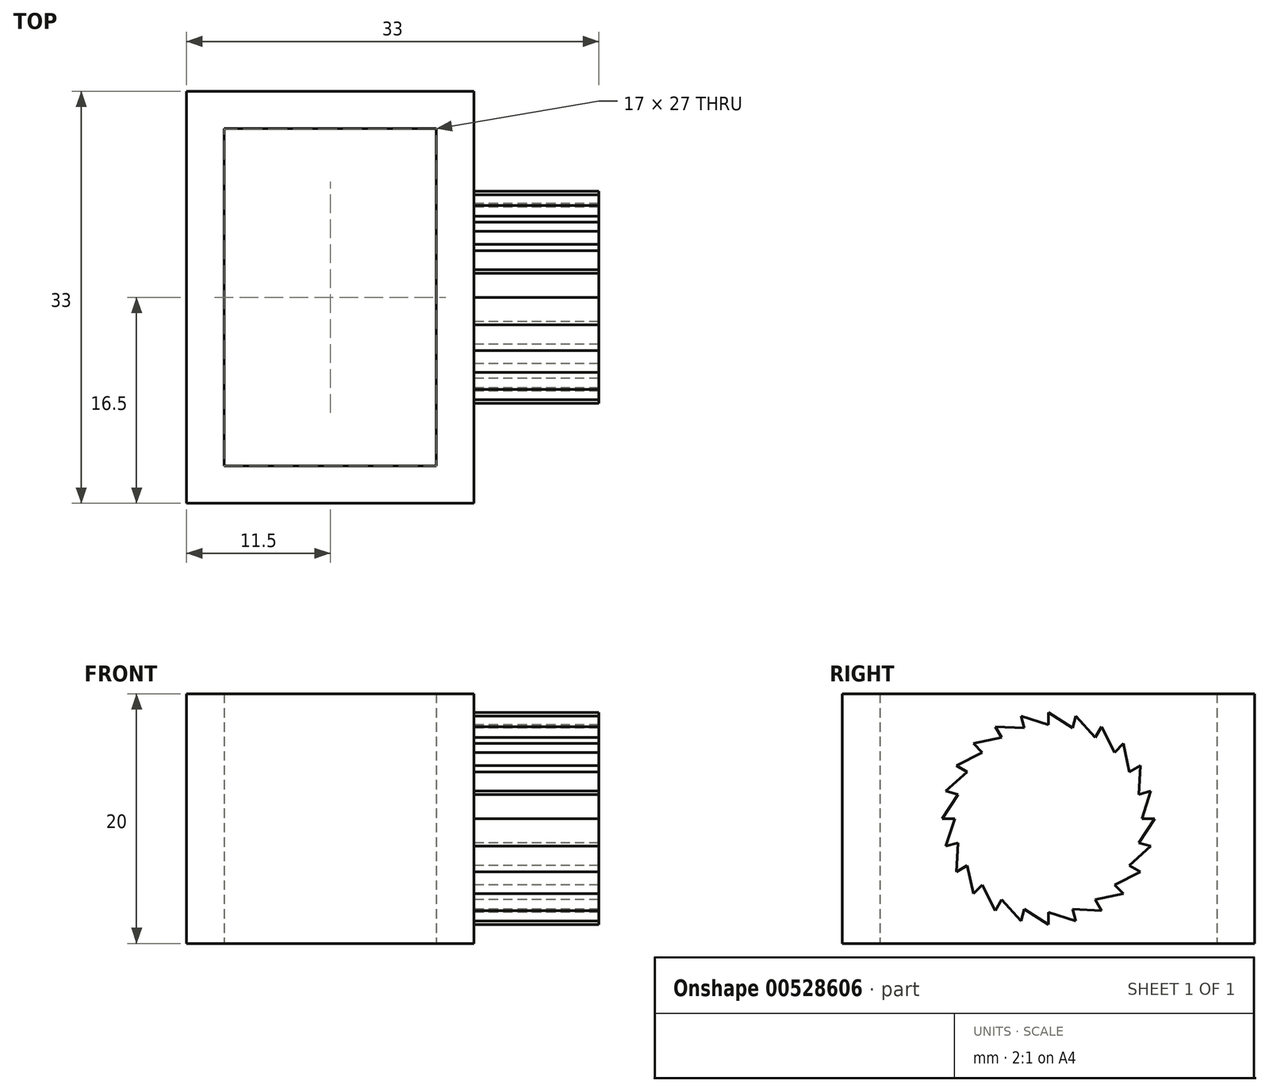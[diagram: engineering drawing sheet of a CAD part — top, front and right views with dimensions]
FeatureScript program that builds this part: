
annotation { "Feature Type Name" : "Feature", "Feature Type Description" : "" }
export const myFeature = defineFeature(function(context is Context, id is Id, definition is map)
    precondition{}
    {
        {
            var Q0;
            Q0=qCreatedBy(makeId("Top.planeOp"),FACE);
            var sketch = newSketch(context, id + "F0", { "sketchPlane" : qUnion([Q0])});
            skLineSegment(sketch, "E0.bottom", {"start": v(3, 3) * mm, "end": v(20, 3) * mm});
            skLineSegment(sketch, "E0.top", {"start": v(3, 30) * mm, "end": v(20, 30) * mm});
            skLineSegment(sketch, "E0.left", {"start": v(3, 3) * mm, "end": v(3, 30) * mm});
            skLineSegment(sketch, "E0.right", {"start": v(20, 3) * mm, "end": v(20, 30) * mm});
            skLineSegment(sketch, "E1.0", {"start": v(23, 0) * mm, "end": v(23, 33) * mm});
            skLineSegment(sketch, "E1.1", {"start": v(0, 0) * mm, "end": v(23, 0) * mm});
            skLineSegment(sketch, "E1.2", {"start": v(0, 0) * mm, "end": v(0, 33) * mm});
            skLineSegment(sketch, "E1.3", {"start": v(0, 33) * mm, "end": v(23, 33) * mm});
            skSolve(sketch);
        }
        {
            var Q0;
            Q0=makeQuery(id+"F0.imprint","IMPRINT",FACE,{"disambiguationData":[TD([[makeQuery(id+"F0.imprint","IMPRINT",EDGE,{"derivedFrom":sQuery(id+"F0.wireOp",EDGE,"E0.bottom")}),-1.0]])]});
            extrude(context, id + "F1", {"entities" : qUnion([Q0]), "depth" : 20 * mm, "offsetDistance" : 25 * mm});
        }
        {
            var Q0;
            Q0=makeQuery(id+"F1.opExtrude","SWEPT_FACE",FACE,{"disambiguationData":[OSD([sQuery(id+"F0.wireOp",EDGE,"E1.0")])]});
            var sketch = newSketch(context, id + "F2", { "sketchPlane" : qUnion([Q0])});
            skCircle(sketch, "E2", {"center": v(16.5, 10) * mm, "radius": 7.5 * mm});
            skLineSegment(sketch, "E3", {"start": v(16.5, 17.5) * mm, "end": v(16.5, 18.5) * mm});
            skLineSegment(sketch, "E4", {"start": v(16.5, 18.5) * mm, "end": v(18.44, 17.24) * mm});
            skLineSegment(sketch, "E5.1.0", {"start": v(18.7, 18.21) * mm, "end": v(20.25, 16.5) * mm});
            skLineSegment(sketch, "E5.1.1", {"start": v(18.44, 17.24) * mm, "end": v(18.7, 18.21) * mm});
            skLineSegment(sketch, "E5.2.0", {"start": v(20.75, 17.36) * mm, "end": v(21.8, 15.3) * mm});
            skLineSegment(sketch, "E5.2.1", {"start": v(20.25, 16.5) * mm, "end": v(20.75, 17.36) * mm});
            skLineSegment(sketch, "E5.3.0", {"start": v(22.51, 16.01) * mm, "end": v(23, 13.75) * mm});
            skLineSegment(sketch, "E5.3.1", {"start": v(21.8, 15.3) * mm, "end": v(22.51, 16.01) * mm});
            skLineSegment(sketch, "E5.4.0", {"start": v(23.86, 14.25) * mm, "end": v(23.74, 11.94) * mm});
            skLineSegment(sketch, "E5.4.1", {"start": v(23, 13.75) * mm, "end": v(23.86, 14.25) * mm});
            skLineSegment(sketch, "E5.5.0", {"start": v(24.71, 12.2) * mm, "end": v(24, 10) * mm});
            skLineSegment(sketch, "E5.5.1", {"start": v(23.74, 11.94) * mm, "end": v(24.71, 12.2) * mm});
            skLineSegment(sketch, "E5.6.0", {"start": v(25, 10) * mm, "end": v(23.74, 8.06) * mm});
            skLineSegment(sketch, "E5.6.1", {"start": v(24, 10) * mm, "end": v(25, 10) * mm});
            skLineSegment(sketch, "E5.7.0", {"start": v(24.71, 7.8) * mm, "end": v(23, 6.25) * mm});
            skLineSegment(sketch, "E5.7.1", {"start": v(23.74, 8.06) * mm, "end": v(24.71, 7.8) * mm});
            skLineSegment(sketch, "E5.8.0", {"start": v(23.86, 5.75) * mm, "end": v(21.8, 4.7) * mm});
            skLineSegment(sketch, "E5.8.1", {"start": v(23, 6.25) * mm, "end": v(23.86, 5.75) * mm});
            skLineSegment(sketch, "E5.9.0", {"start": v(22.51, 3.99) * mm, "end": v(20.25, 3.5) * mm});
            skLineSegment(sketch, "E5.9.1", {"start": v(21.8, 4.7) * mm, "end": v(22.51, 3.99) * mm});
            skLineSegment(sketch, "E5.10.0", {"start": v(20.75, 2.64) * mm, "end": v(18.44, 2.76) * mm});
            skLineSegment(sketch, "E5.10.1", {"start": v(20.25, 3.5) * mm, "end": v(20.75, 2.64) * mm});
            skLineSegment(sketch, "E5.11.0", {"start": v(18.7, 1.79) * mm, "end": v(16.5, 2.5) * mm});
            skLineSegment(sketch, "E5.11.1", {"start": v(18.44, 2.76) * mm, "end": v(18.7, 1.79) * mm});
            skLineSegment(sketch, "E5.12.0", {"start": v(16.5, 1.5) * mm, "end": v(14.56, 2.76) * mm});
            skLineSegment(sketch, "E5.12.1", {"start": v(16.5, 2.5) * mm, "end": v(16.5, 1.5) * mm});
            skLineSegment(sketch, "E5.13.0", {"start": v(14.3, 1.79) * mm, "end": v(12.75, 3.5) * mm});
            skLineSegment(sketch, "E5.13.1", {"start": v(14.56, 2.76) * mm, "end": v(14.3, 1.79) * mm});
            skLineSegment(sketch, "E5.14.0", {"start": v(12.25, 2.64) * mm, "end": v(11.2, 4.7) * mm});
            skLineSegment(sketch, "E5.14.1", {"start": v(12.75, 3.5) * mm, "end": v(12.25, 2.64) * mm});
            skLineSegment(sketch, "E5.15.0", {"start": v(10.49, 3.99) * mm, "end": v(10, 6.25) * mm});
            skLineSegment(sketch, "E5.15.1", {"start": v(11.2, 4.7) * mm, "end": v(10.49, 3.99) * mm});
            skLineSegment(sketch, "E5.16.0", {"start": v(9.14, 5.75) * mm, "end": v(9.26, 8.06) * mm});
            skLineSegment(sketch, "E5.16.1", {"start": v(10, 6.25) * mm, "end": v(9.14, 5.75) * mm});
            skLineSegment(sketch, "E5.17.0", {"start": v(8.29, 7.8) * mm, "end": v(9, 10) * mm});
            skLineSegment(sketch, "E5.17.1", {"start": v(9.26, 8.06) * mm, "end": v(8.29, 7.8) * mm});
            skLineSegment(sketch, "E5.18.0", {"start": v(8, 10) * mm, "end": v(9.26, 11.94) * mm});
            skLineSegment(sketch, "E5.18.1", {"start": v(9, 10) * mm, "end": v(8, 10) * mm});
            skLineSegment(sketch, "E5.19.0", {"start": v(8.29, 12.2) * mm, "end": v(10, 13.75) * mm});
            skLineSegment(sketch, "E5.19.1", {"start": v(9.26, 11.94) * mm, "end": v(8.29, 12.2) * mm});
            skLineSegment(sketch, "E5.20.0", {"start": v(9.14, 14.25) * mm, "end": v(11.2, 15.3) * mm});
            skLineSegment(sketch, "E5.20.1", {"start": v(10, 13.75) * mm, "end": v(9.14, 14.25) * mm});
            skLineSegment(sketch, "E5.21.0", {"start": v(10.49, 16.01) * mm, "end": v(12.75, 16.5) * mm});
            skLineSegment(sketch, "E5.21.1", {"start": v(11.2, 15.3) * mm, "end": v(10.49, 16.01) * mm});
            skLineSegment(sketch, "E5.22.0", {"start": v(12.25, 17.36) * mm, "end": v(14.56, 17.24) * mm});
            skLineSegment(sketch, "E5.22.1", {"start": v(12.75, 16.5) * mm, "end": v(12.25, 17.36) * mm});
            skLineSegment(sketch, "E5.anchor1", {"start": v(16.5, 10) * mm, "end": v(16.5, 17.5) * mm, "construction": true});
            skLineSegment(sketch, "E5.anchor2", {"start": v(16.5, 10) * mm, "end": v(14.56, 17.24) * mm, "construction": true});
            skLineSegment(sketch, "E6.3.23.0", {"start": v(14.56, 17.24) * mm, "end": v(14.3, 18.21) * mm});
            skLineSegment(sketch, "E6.4.23.0", {"start": v(14.3, 18.21) * mm, "end": v(16.5, 17.5) * mm});
            skSolve(sketch);
        }
        {
            var Q0;
            Q0 = qSketchRegion(id + "F2", true);
            extrude(context, id + "F3", {"entities" : qUnion([Q0]), "operationType" : NewBodyOperationType.ADD, "depth" : 10 * mm, "offsetDistance" : 25 * mm});
        }
    });
